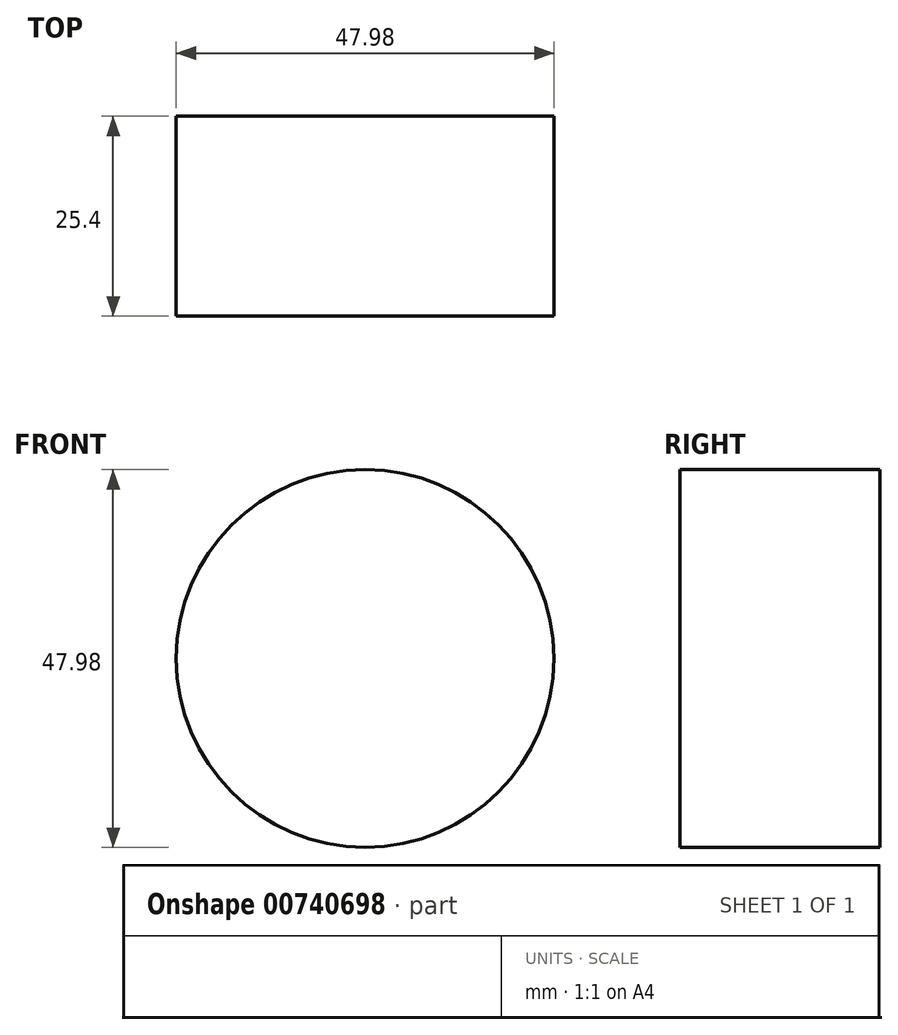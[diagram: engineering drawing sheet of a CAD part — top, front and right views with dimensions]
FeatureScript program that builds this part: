
annotation { "Feature Type Name" : "Feature", "Feature Type Description" : "" }
export const myFeature = defineFeature(function(context is Context, id is Id, definition is map)
    precondition{}
    {
        {
            var Q0;
            Q0=qCreatedBy(makeId("Front.planeOp"),FACE);
            var sketch = newSketch(context, id + "F0", { "sketchPlane" : qUnion([Q0])});
            skCircle(sketch, "E0", {"center": v(0, 0) * mm, "radius": 23.99 * mm});
            skSolve(sketch);
        }
        {
            var Q0;
            Q0=makeQuery(id+"F0.imprint","IMPRINT",FACE,{"disambiguationData":[TD([[makeQuery(id+"F0.imprint","IMPRINT",EDGE,{"derivedFrom":sQuery(id+"F0.wireOp",EDGE,"E0")}),1.0]])]});
            extrude(context, id + "F1", {"entities" : qUnion([Q0]), "depth" : 25.4 * mm, "offsetDistance" : 25.4 * mm});
        }
    });
